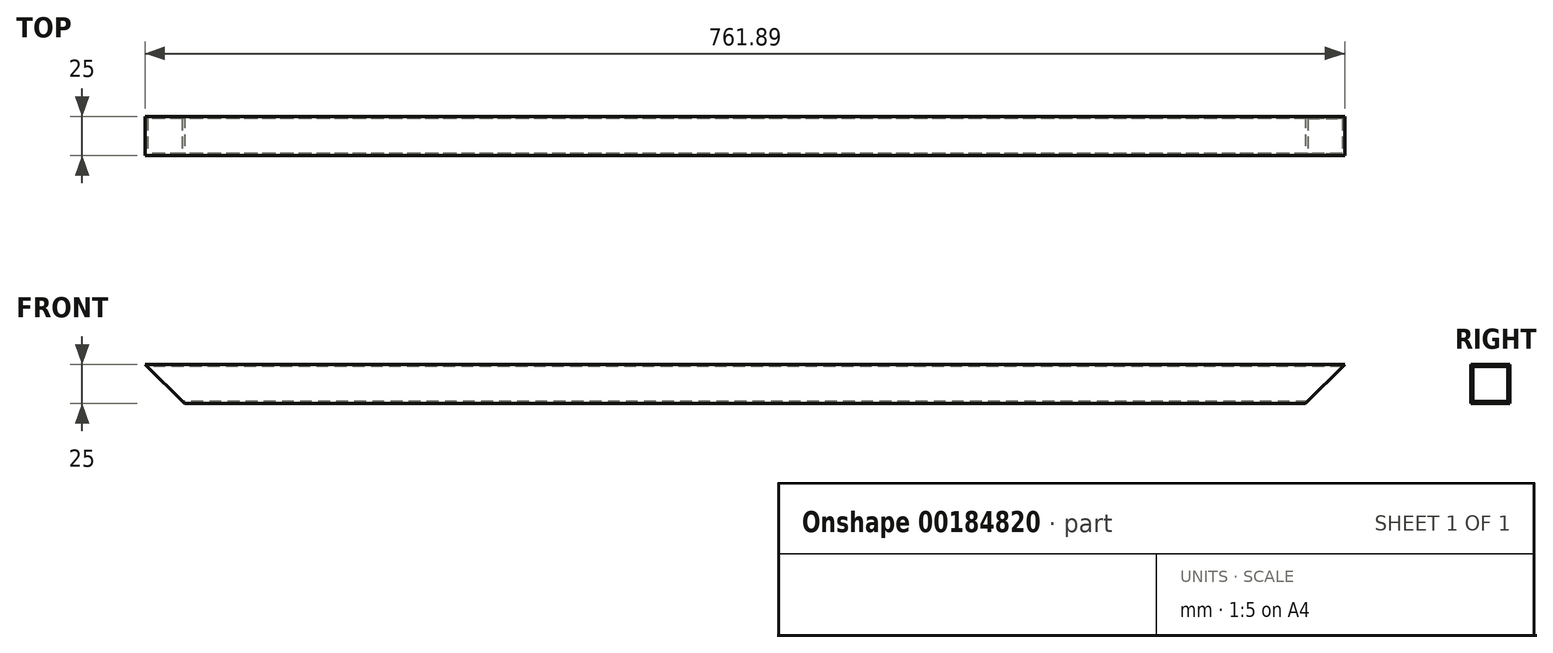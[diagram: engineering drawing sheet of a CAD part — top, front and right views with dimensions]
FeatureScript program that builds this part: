
annotation { "Feature Type Name" : "Feature", "Feature Type Description" : "" }
export const myFeature = defineFeature(function(context is Context, id is Id, definition is map)
    precondition{}
    {
        {
            var Q0;
            Q0=qCreatedBy(makeId("Right.planeOp"),FACE);
            var sketch = newSketch(context, id + "F0", { "sketchPlane" : qUnion([Q0])});
            skLineSegment(sketch, "E0.bottom", {"start": v(12.5, 12.5) * mm, "end": v(-12.5, 12.5) * mm});
            skLineSegment(sketch, "E0.top", {"start": v(12.5, -12.5) * mm, "end": v(-12.5, -12.5) * mm});
            skLineSegment(sketch, "E0.left", {"start": v(12.5, 12.5) * mm, "end": v(12.5, -12.5) * mm});
            skLineSegment(sketch, "E0.right", {"start": v(-12.5, 12.5) * mm, "end": v(-12.5, -12.5) * mm});
            skPoint(sketch, "E0.middle", {"position": v(0, 0) * mm});
            skSolve(sketch);
        }
        {
            var Q0;
            Q0 = qSketchRegion(id + "F0", true);
            extrude(context, id + "F1", {"entities" : qUnion([Q0]), "depth" : 762 * mm});
        }
        {
            var Q0;
            Q0=qCreatedBy(makeId("Front.planeOp"),FACE);
            var sketch = newSketch(context, id + "F2", { "sketchPlane" : qUnion([Q0])});
            skLineSegment(sketch, "E1", {"start": v(0, 12.6) * mm, "end": v(35.35, -22.75) * mm});
            skLineSegment(sketch, "E2", {"start": v(762, 12.5) * mm, "end": v(732.64, -16.86) * mm});
            skLineSegment(sketch, "E3", {"start": v(0, 12.6) * mm, "end": v(0, -26.69) * mm});
            skLineSegment(sketch, "E4", {"start": v(0, -26.69) * mm, "end": v(35.35, -22.75) * mm});
            skLineSegment(sketch, "E5", {"start": v(762, 12.5) * mm, "end": v(762, -22.75) * mm});
            skLineSegment(sketch, "E6", {"start": v(762, -22.75) * mm, "end": v(732.64, -16.86) * mm});
            skSolve(sketch);
        }
        {
            var Q0;
            Q0=makeQuery(id+"F2.imprint","IMPRINT",FACE,{"disambiguationData":[TD([[makeQuery(id+"F2.imprint","IMPRINT",EDGE,{"derivedFrom":sQuery(id+"F2.wireOp",EDGE,"E1")}),-1.0]])]});
            var Q1;
            Q1=makeQuery(id+"F2.imprint","IMPRINT",FACE,{"disambiguationData":[TD([[makeQuery(id+"F2.imprint","IMPRINT",EDGE,{"derivedFrom":sQuery(id+"F2.wireOp",EDGE,"E2")}),1.0]])]});
            extrude(context, id + "F3", {"entities" : qUnion([Q0, Q1]), "operationType" : NewBodyOperationType.REMOVE, "endBound" : BoundingType.SYMMETRIC, "depth" : 25 * mm});
        }
        {
            var Q0;
            Q0=qCreatedBy(makeId("Right.planeOp"),FACE);
            var sketch = newSketch(context, id + "F4", { "sketchPlane" : qUnion([Q0])});
            skLineSegment(sketch, "E7.bottom", {"start": v(-11, 11) * mm, "end": v(11, 11) * mm});
            skLineSegment(sketch, "E7.top", {"start": v(-11, -11) * mm, "end": v(11, -11) * mm});
            skLineSegment(sketch, "E7.left", {"start": v(-11, 11) * mm, "end": v(-11, -11) * mm});
            skLineSegment(sketch, "E7.right", {"start": v(11, 11) * mm, "end": v(11, -11) * mm});
            skPoint(sketch, "E7.middle", {"position": v(0, 0) * mm});
            skSolve(sketch);
        }
        {
            var Q0;
            Q0=makeQuery(id+"F4.imprint","IMPRINT",FACE,{"disambiguationData":[TD([[makeQuery(id+"F4.imprint","IMPRINT",EDGE,{"derivedFrom":sQuery(id+"F4.wireOp",EDGE,"E7.bottom")}),-1.0]])]});
            var Q1;
            Q1=makeQuery(id+"F3.boolean.opBoolean","COPY",FACE,{"derivedFrom":makeQuery(id+"F3.opExtrude","SWEPT_FACE",FACE,{"disambiguationData":[OSD([sQuery(id+"F2.wireOp",EDGE,"E2")])]})});
            extrude(context, id + "F5", {"entities" : qUnion([Q0]), "operationType" : NewBodyOperationType.REMOVE, "endBound" : BoundingType.THROUGH_ALL, "endBoundEntityFace" : qUnion([Q1]), "depth" : 750 * mm});
        }
    });
